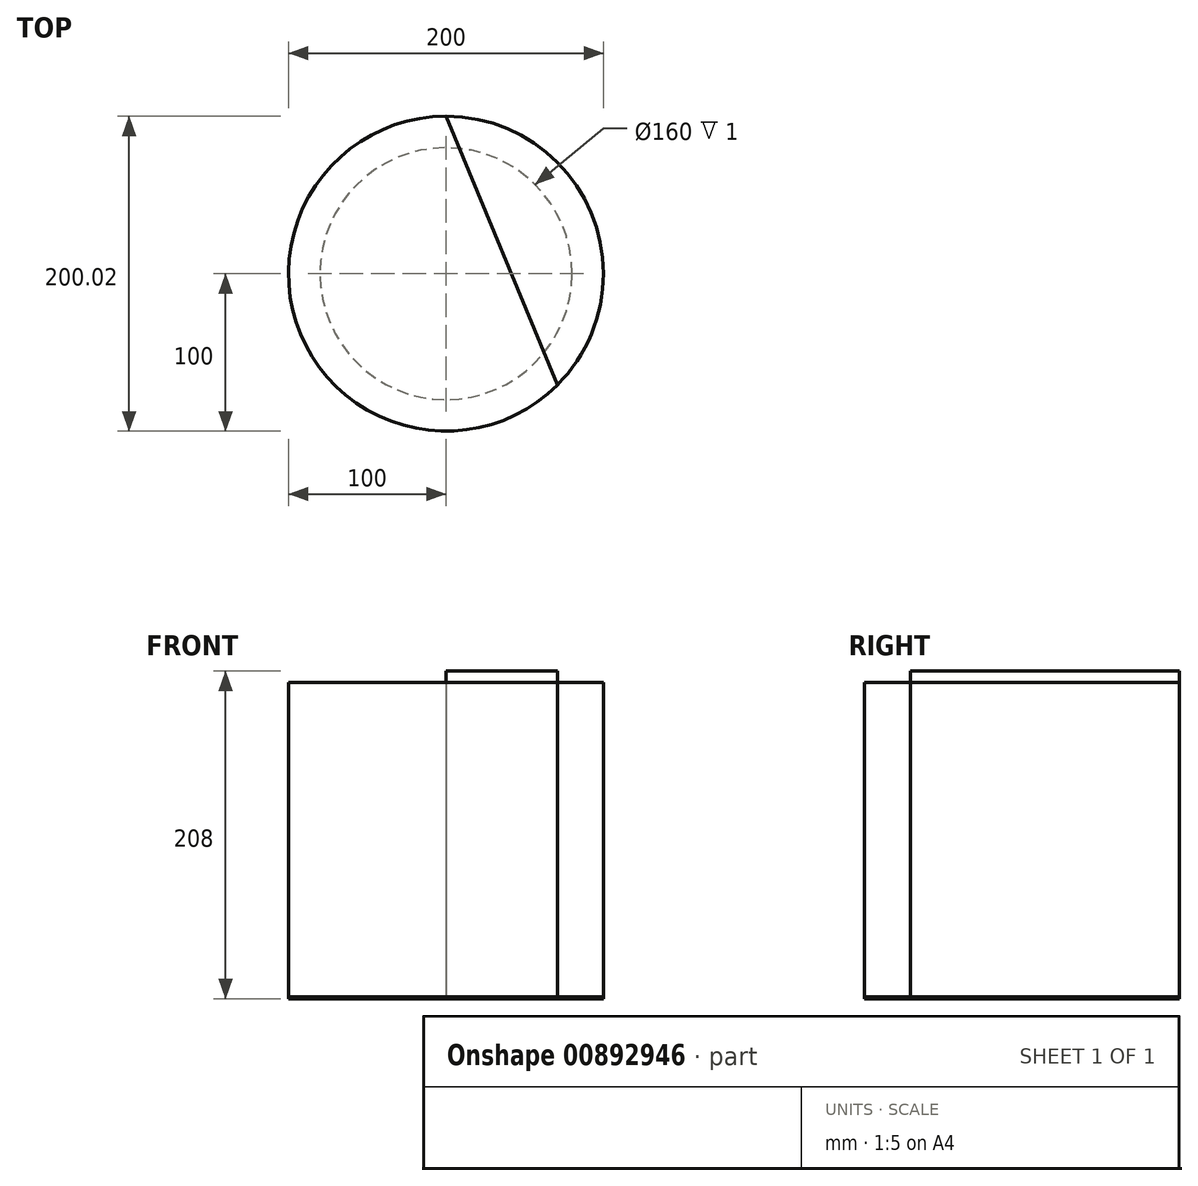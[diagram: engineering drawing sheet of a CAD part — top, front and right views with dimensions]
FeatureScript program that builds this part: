
annotation { "Feature Type Name" : "Feature", "Feature Type Description" : "" }
export const myFeature = defineFeature(function(context is Context, id is Id, definition is map)
    precondition{}
    {
        {
            var Q0;
            Q0=qCreatedBy(makeId("Top.planeOp"),FACE);
            cPlane(context, id + "F0", {"entities" : qUnion([Q0]), "cplaneType" : CPlaneType.OFFSET, "offset" : 200 * mm, "oppositeDirection" : true, "width" : 150 * mm, "height" : 150 * mm});
        }
        {
            var Q0;
            Q0=qCreatedBy(makeId("Top.planeOp"),FACE);
            var sketch = newSketch(context, id + "F1", { "sketchPlane" : qUnion([Q0])});
            skCircle(sketch, "E0", {"center": v(0, 0) * mm, "radius": 100 * mm});
            skLineSegment(sketch, "E1.bottom", {"start": v(-100, 100) * mm, "end": v(100, 100) * mm, "construction": true});
            skLineSegment(sketch, "E1.top", {"start": v(-100, -100) * mm, "end": v(100, -100) * mm, "construction": true});
            skLineSegment(sketch, "E1.left", {"start": v(-100, 100) * mm, "end": v(-100, -100) * mm, "construction": true});
            skLineSegment(sketch, "E1.right", {"start": v(100, 100) * mm, "end": v(100, -100) * mm, "construction": true});
            skLineSegment(sketch, "E2", {"start": v(-70.71, 70.71) * mm, "end": v(-70.71, 100) * mm, "construction": true});
            skLineSegment(sketch, "E3", {"start": v(-70.71, 70.71) * mm, "end": v(-100, 70.71) * mm, "construction": true});
            skLineSegment(sketch, "E4", {"start": v(-70.71, 70.71) * mm, "end": v(100, 70.71) * mm, "construction": true});
            skLineSegment(sketch, "E5", {"start": v(-70.71, 70.71) * mm, "end": v(-70.71, -100) * mm, "construction": true});
            skLineSegment(sketch, "E6", {"start": v(-70.71, -70.71) * mm, "end": v(100, -70.71) * mm, "construction": true});
            skLineSegment(sketch, "E7", {"start": v(70.71, 70.71) * mm, "end": v(70.71, -70.71) * mm, "construction": true});
            skLineSegment(sketch, "E8", {"start": v(70.71, -70.71) * mm, "end": v(70.71, -100) * mm, "construction": true});
            skLineSegment(sketch, "E9", {"start": v(70.71, 70.71) * mm, "end": v(70.71, 100) * mm, "construction": true});
            skLineSegment(sketch, "E10", {"start": v(-70.71, -70.71) * mm, "end": v(-100, -70.71) * mm, "construction": true});
            skCircle(sketch, "E11", {"center": v(0, 0) * mm, "radius": 80 * mm});
            skLineSegment(sketch, "E12", {"start": v(100, 0) * mm, "end": v(-70.71, -70.71) * mm, "construction": true});
            skLineSegment(sketch, "E13", {"start": v(-70.71, -70.71) * mm, "end": v(0, 100) * mm, "construction": true});
            skLineSegment(sketch, "E14", {"start": v(0, 100) * mm, "end": v(70.71, -70.71) * mm, "construction": true});
            skLineSegment(sketch, "E15", {"start": v(70.71, -70.71) * mm, "end": v(-100, 0) * mm, "construction": true});
            skLineSegment(sketch, "E16", {"start": v(-100, 0) * mm, "end": v(70.71, 70.71) * mm, "construction": true});
            skLineSegment(sketch, "E17", {"start": v(70.71, 70.71) * mm, "end": v(0, -100) * mm, "construction": true});
            skLineSegment(sketch, "E18", {"start": v(0, -100) * mm, "end": v(-70.71, 70.71) * mm, "construction": true});
            skLineSegment(sketch, "E19", {"start": v(-70.18, 70.56) * mm, "end": v(100, 0) * mm, "construction": true});
            skCircle(sketch, "E20", {"center": v(0, 0) * mm, "radius": 38.33 * mm});
            skLineSegment(sketch, "E21", {"start": v(0, 38.33) * mm, "end": v(100, 38.33) * mm, "construction": true});
            skLineSegment(sketch, "E22", {"start": v(38.33, 0) * mm, "end": v(38.33, 100) * mm, "construction": true});
            skLineSegment(sketch, "E23", {"start": v(0, -38.33) * mm, "end": v(100, -38.33) * mm, "construction": true});
            skLineSegment(sketch, "E24", {"start": v(38.33, 0) * mm, "end": v(38.33, -70.22) * mm, "construction": true});
            skSolve(sketch);
        }
        {
            var Q0;
            Q0=qCreatedBy(id+"F0.planeOp",FACE);
            var sketch = newSketch(context, id + "F2", { "sketchPlane" : qUnion([Q0])});
            skCircle(sketch, "E25", {"center": v(0, 0) * mm, "radius": 100 * mm});
            skLineSegment(sketch, "E26.bottom", {"start": v(-100, 100) * mm, "end": v(100, 100) * mm, "construction": true});
            skLineSegment(sketch, "E26.top", {"start": v(-100, -100) * mm, "end": v(100, -100) * mm, "construction": true});
            skLineSegment(sketch, "E26.left", {"start": v(-100, 100) * mm, "end": v(-100, -100) * mm, "construction": true});
            skLineSegment(sketch, "E26.right", {"start": v(100, 100) * mm, "end": v(100, -100) * mm, "construction": true});
            skLineSegment(sketch, "E27", {"start": v(0, 100) * mm, "end": v(0, -100) * mm, "construction": true});
            skLineSegment(sketch, "E28", {"start": v(-100, 0) * mm, "end": v(100, 0) * mm, "construction": true});
            skLineSegment(sketch, "E29", {"start": v(-100, 100) * mm, "end": v(100, -100) * mm, "construction": true});
            skLineSegment(sketch, "E30", {"start": v(100, 100) * mm, "end": v(-100, -100) * mm, "construction": true});
            skLineSegment(sketch, "E31", {"start": v(-70.71, 70.71) * mm, "end": v(-70.71, 100) * mm, "construction": true});
            skLineSegment(sketch, "E32", {"start": v(-70.71, 70.71) * mm, "end": v(-100, 70.71) * mm, "construction": true});
            skLineSegment(sketch, "E33", {"start": v(-70.71, 70.71) * mm, "end": v(100, 70.71) * mm, "construction": true});
            skLineSegment(sketch, "E34", {"start": v(-70.71, 70.71) * mm, "end": v(-70.71, -100) * mm, "construction": true});
            skLineSegment(sketch, "E35", {"start": v(-70.71, -70.71) * mm, "end": v(100, -70.71) * mm, "construction": true});
            skLineSegment(sketch, "E36", {"start": v(70.71, 70.71) * mm, "end": v(70.71, -70.71) * mm, "construction": true});
            skLineSegment(sketch, "E37", {"start": v(70.71, -70.71) * mm, "end": v(70.71, -100) * mm, "construction": true});
            skLineSegment(sketch, "E38", {"start": v(70.71, 70.71) * mm, "end": v(70.71, 100) * mm, "construction": true});
            skLineSegment(sketch, "E39", {"start": v(-70.71, -70.71) * mm, "end": v(-100, -70.71) * mm, "construction": true});
            skCircle(sketch, "E40", {"center": v(0, 0) * mm, "radius": 80 * mm});
            skSolve(sketch);
        }
        {
            var Q0;
            Q0=qCreatedBy(id+"F0.planeOp",FACE);
            var sketch = newSketch(context, id + "F3", { "sketchPlane" : qUnion([Q0])});
            skLineSegment(sketch, "E41", {"start": v(0, 100) * mm, "end": v(70.71, -70.71) * mm});
            skLineSegment(sketch, "E42.0", {"start": v(0.05, 100.02) * mm, "end": v(70.76, -70.7) * mm});
            skLineSegment(sketch, "E43", {"start": v(70.71, -70.71) * mm, "end": v(70.76, -70.71) * mm});
            skLineSegment(sketch, "E44", {"start": v(70.76, -70.71) * mm, "end": v(70.76, -70.7) * mm});
            skLineSegment(sketch, "E45", {"start": v(0.05, 100.02) * mm, "end": v(0, 100.02) * mm});
            skLineSegment(sketch, "E46", {"start": v(0, 100.02) * mm, "end": v(0, 100) * mm});
            skSolve(sketch);
        }
        {
            var Q0;
            Q0=makeQuery(id+"F3.imprint","IMPRINT",FACE,{"disambiguationData":[TD([[makeQuery(id+"F3.imprint","IMPRINT",EDGE,{"derivedFrom":sQuery(id+"F3.wireOp",EDGE,"E41")}),1.0]])]});
            extrude(context, id + "F4", {"entities" : qUnion([Q0]), "depth" : 207 * mm, "offsetDistance" : 25 * mm});
        }
        {
            var Q0;
            Q0=makeQuery(id+"F4.opExtrude","SWEPT_FACE",FACE,{"disambiguationData":[OSD([sQuery(id+"F3.wireOp",EDGE,"E42.0")])]});
            cPlane(context, id + "F5", {"entities" : qUnion([Q0]), "cplaneType" : CPlaneType.OFFSET, "offset" : 0 * mm, "width" : 150 * mm, "height" : 150 * mm});
        }
        {
            var Q0;
            Q0=makeQuery(id+"F2.imprint","IMPRINT",FACE,{"disambiguationData":[TD([[makeQuery(id+"F2.imprint","IMPRINT",EDGE,{"derivedFrom":sQuery(id+"F2.wireOp",EDGE,"E25")}),1.0]])]});
            var Q1;
            Q1=makeQuery(id+"F2.imprint","IMPRINT",FACE,{"disambiguationData":[TD([[makeQuery(id+"F2.imprint","IMPRINT",EDGE,{"derivedFrom":sQuery(id+"F2.wireOp",EDGE,"E40")}),1.0]])]});
            extrude(context, id + "F6", {"entities" : qUnion([Q0, Q1]), "depth" : 200 * mm, "offsetDistance" : 25 * mm});
        }
        {
            var Q0;
            Q0=makeQuery(id+"F2.imprint","IMPRINT",FACE,{"disambiguationData":[TD([[makeQuery(id+"F2.imprint","IMPRINT",EDGE,{"derivedFrom":sQuery(id+"F2.wireOp",EDGE,"E25")}),1.0]])]});
            extrude(context, id + "F7", {"entities" : qUnion([Q0]), "oppositeDirection" : true, "depth" : 1 * mm, "offsetDistance" : 25 * mm});
        }
    });
